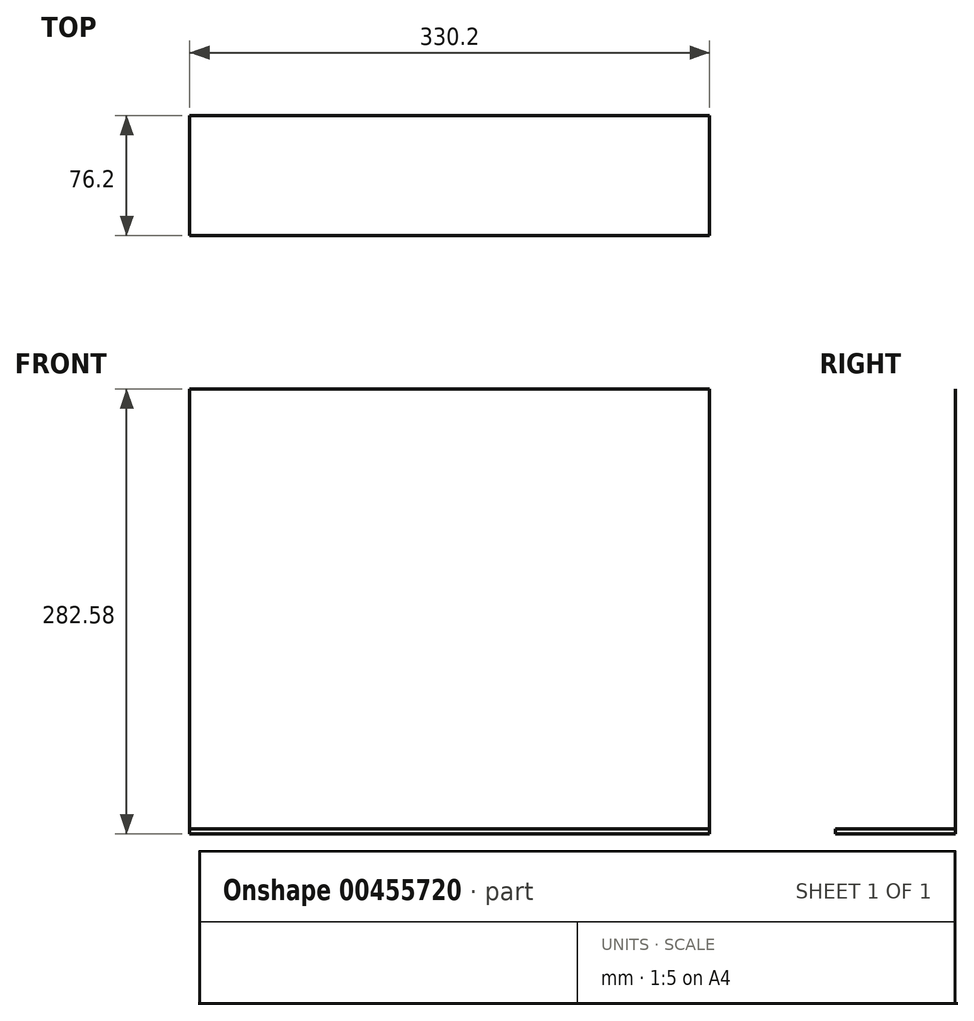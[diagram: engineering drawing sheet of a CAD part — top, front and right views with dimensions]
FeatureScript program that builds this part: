
annotation { "Feature Type Name" : "Feature", "Feature Type Description" : "" }
export const myFeature = defineFeature(function(context is Context, id is Id, definition is map)
    precondition{}
    {
        {
            var Q0;
            Q0=qCreatedBy(makeId("Top.planeOp"),FACE);
            var sketch = newSketch(context, id + "F0", { "sketchPlane" : qUnion([Q0])});
            skLineSegment(sketch, "E0.bottom", {"start": v(-165.1, 38.1) * mm, "end": v(165.1, 38.1) * mm});
            skLineSegment(sketch, "E0.top", {"start": v(-165.1, -38.1) * mm, "end": v(165.1, -38.1) * mm});
            skLineSegment(sketch, "E0.left", {"start": v(-165.1, 38.1) * mm, "end": v(-165.1, -38.1) * mm});
            skLineSegment(sketch, "E0.right", {"start": v(165.1, 38.1) * mm, "end": v(165.1, -38.1) * mm});
            skPoint(sketch, "E0.middle", {"position": v(0, 0) * mm});
            skSolve(sketch);
        }
        {
            var Q0;
            Q0 = qSketchRegion(id + "F0", true);
            extrude(context, id + "F1", {"entities" : qUnion([Q0]), "depth" : 3.17 * mm});
        }
        {
            var Q0;
            Q0=makeQuery(id+"F1.opExtrude","SWEPT_FACE",FACE,{"disambiguationData":[OSD([sQuery(id+"F0.wireOp",EDGE,"E0.bottom")])]});
            var sketch = newSketch(context, id + "F2", { "sketchPlane" : qUnion([Q0])});
            skLineSegment(sketch, "E1.bottom", {"start": v(-165.1, 0) * mm, "end": v(165.1, 0) * mm});
            skLineSegment(sketch, "E1.top", {"start": v(-165.1, 282.58) * mm, "end": v(165.1, 282.58) * mm});
            skLineSegment(sketch, "E1.left", {"start": v(-165.1, 0) * mm, "end": v(-165.1, 282.58) * mm});
            skLineSegment(sketch, "E1.right", {"start": v(165.1, 0) * mm, "end": v(165.1, 282.58) * mm});
            skSolve(sketch);
        }
        {
            var Q0;
            Q0 = qSketchRegion(id + "F2", true);
            extrude(context, id + "F3", {"entities" : qUnion([Q0]), "operationType" : NewBodyOperationType.ADD, "depth" : 1 / 203.2 * mm});
        }
    });
